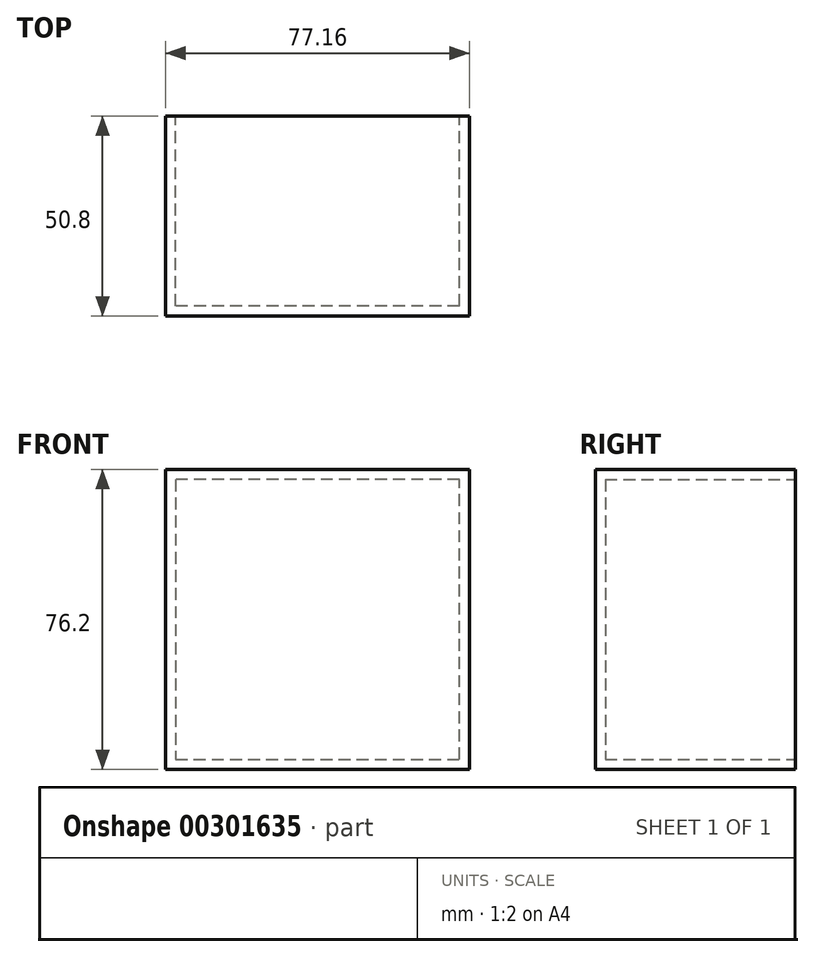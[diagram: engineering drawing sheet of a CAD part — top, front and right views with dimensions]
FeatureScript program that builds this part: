
annotation { "Feature Type Name" : "Feature", "Feature Type Description" : "" }
export const myFeature = defineFeature(function(context is Context, id is Id, definition is map)
    precondition{}
    {
        {
            var Q0;
            Q0=qCreatedBy(makeId("Front.planeOp"),FACE);
            var sketch = newSketch(context, id + "F0", { "sketchPlane" : qUnion([Q0])});
            skLineSegment(sketch, "E0", {"start": v(-55.17, 45.47) * mm, "end": v(-55.17, -30.73) * mm});
            skLineSegment(sketch, "E1", {"start": v(-55.17, -30.73) * mm, "end": v(21.99, -30.73) * mm});
            skLineSegment(sketch, "E2", {"start": v(21.99, -30.73) * mm, "end": v(21.99, 45.47) * mm});
            skLineSegment(sketch, "E3", {"start": v(21.99, 45.47) * mm, "end": v(-55.17, 45.47) * mm});
            skSolve(sketch);
        }
        {
            var Q0;
            Q0=makeQuery(id+"F0.imprint","IMPRINT",FACE,{"disambiguationData":[TD([[makeQuery(id+"F0.imprint","IMPRINT",EDGE,{"derivedFrom":sQuery(id+"F0.wireOp",EDGE,"E0")}),1.0]])]});
            extrude(context, id + "F1", {"entities" : qUnion([Q0]), "depth" : 50.8 * mm});
        }
        {
            var Q0;
            Q0=makeQuery(id+"F1.opExtrude","CAP_FACE",FACE,{"disambiguationData":[OSD([sQuery(id+"F0.wireOp",EDGE,"E0"),sQuery(id+"F0.wireOp",EDGE,"E1"),sQuery(id+"F0.wireOp",EDGE,"E2"),sQuery(id+"F0.wireOp",EDGE,"E3")])],"isStart":true});
            shell(context, id + "F2", {"entities" : qUnion([Q0]), "thickness" : 2.54 * mm});
        }
    });
